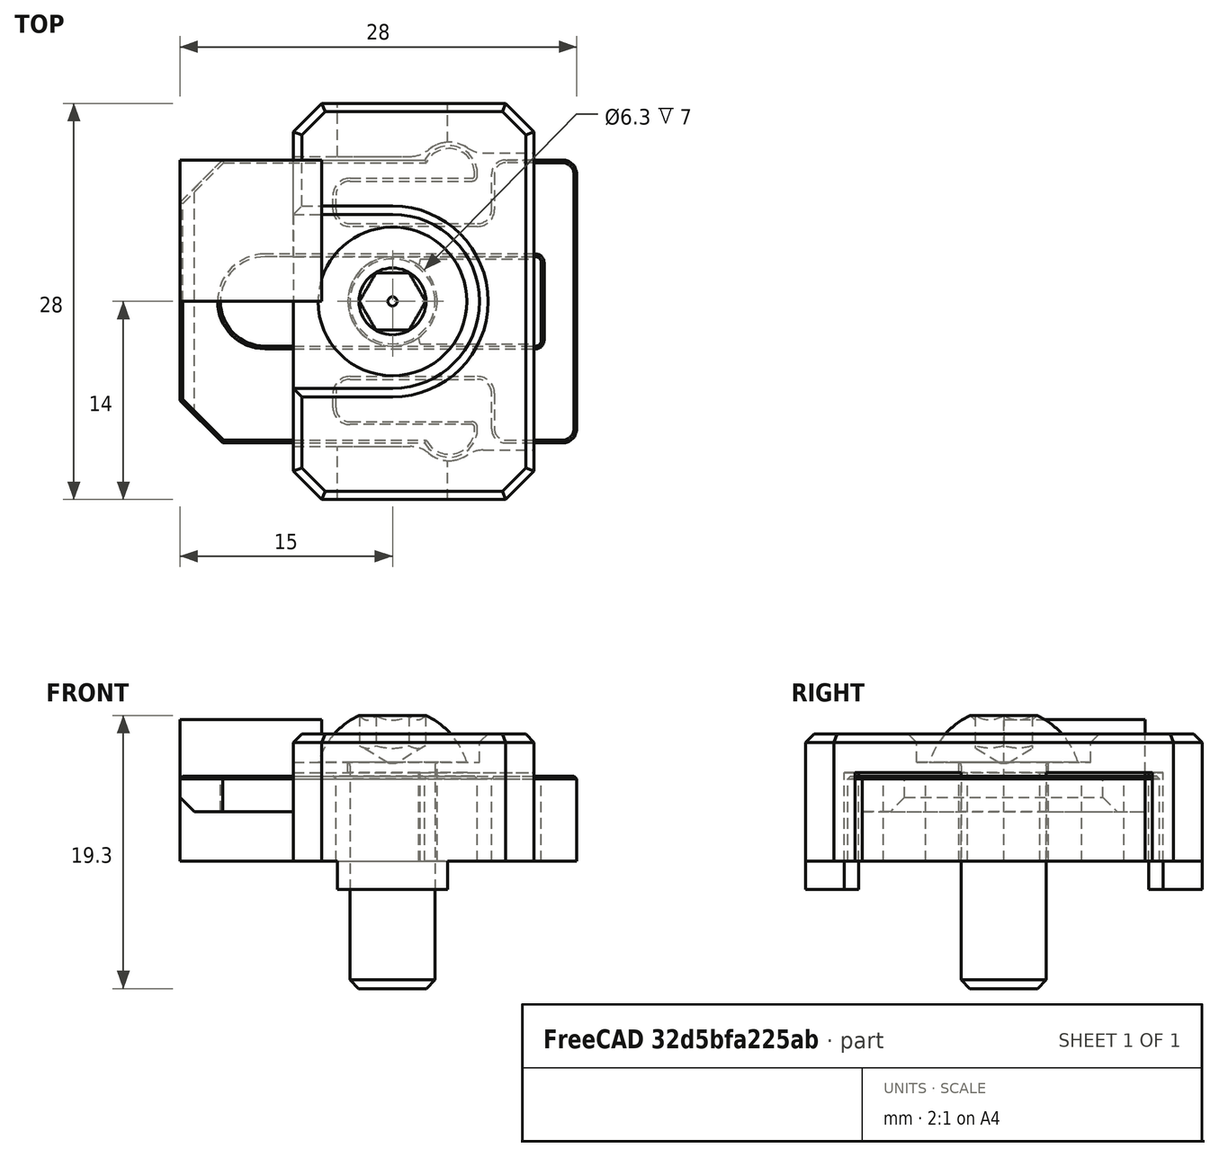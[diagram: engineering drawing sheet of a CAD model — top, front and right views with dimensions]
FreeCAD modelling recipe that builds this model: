
FCSTD DOCUMENT  (FreeCAD 0.19R24291 (Git))
Label: panel-mount-assembly
License: Other
LicenseURL: GPL3
objects: Part::Feature×2, Part::FeaturePython×1, PartDesign::Point×1, Part::Box×1, App::Part×1
note: 5 computed .brp shape members not serialized (recipe doc carries the construction recipe); baked Part::Feature solids carry a one-line shape summary decoded from their .brp

FEATURE [Part::Feature] Chamfer008001001
  shape: bbox 28 x 22 x 6 mm, 82 faces (baked)
FEATURE [Part::Feature] Chamfer008002001001
  shape: bbox 17 x 28 x 11 mm, 53 faces (baked)
FEATURE [Part::FeaturePython] Screw  label="M6x16-Screw"  # Fasteners workbench fastener (typed FeaturePython)
  Placement = pos=(15,0,7) rot=(0,0,1;0rad)
  baseObject = -> Chamfer008002001001 [Edge135]
  diameter = 4
  invert = false
  length = 3
  lengthCustom = 16
  matchOuter = false
  offset = 0
  thread = false
  type = 40
FEATURE [PartDesign::Point] Point_Panel_mounterr2_000_1  label="Point_Panel-mounterr2-000_1"
  AttacherType = Attacher::AttachEnginePoint
  AttachmentOffset = pos=(0,5,0) rot=(0,0,1;0rad)
  MapMode = 36
  Placement = pos=(15,1.1e-15,-4) rot=(1,0,0;1.5708rad)
  Support = -> [Screw]
FEATURE [Part::Box] Box  label="Cube"
  AttacherType = Attacher::AttachEngine3D
  Height = 10
  Length = 10
  Width = 10
FEATURE [App::Part] Part  label="Panel-mounterr2-000"
  Group = -> [Chamfer008001001,Chamfer008002001001,Screw,Point_Panel_mounterr2_000_1,Box]
  Origin = -> Origin
